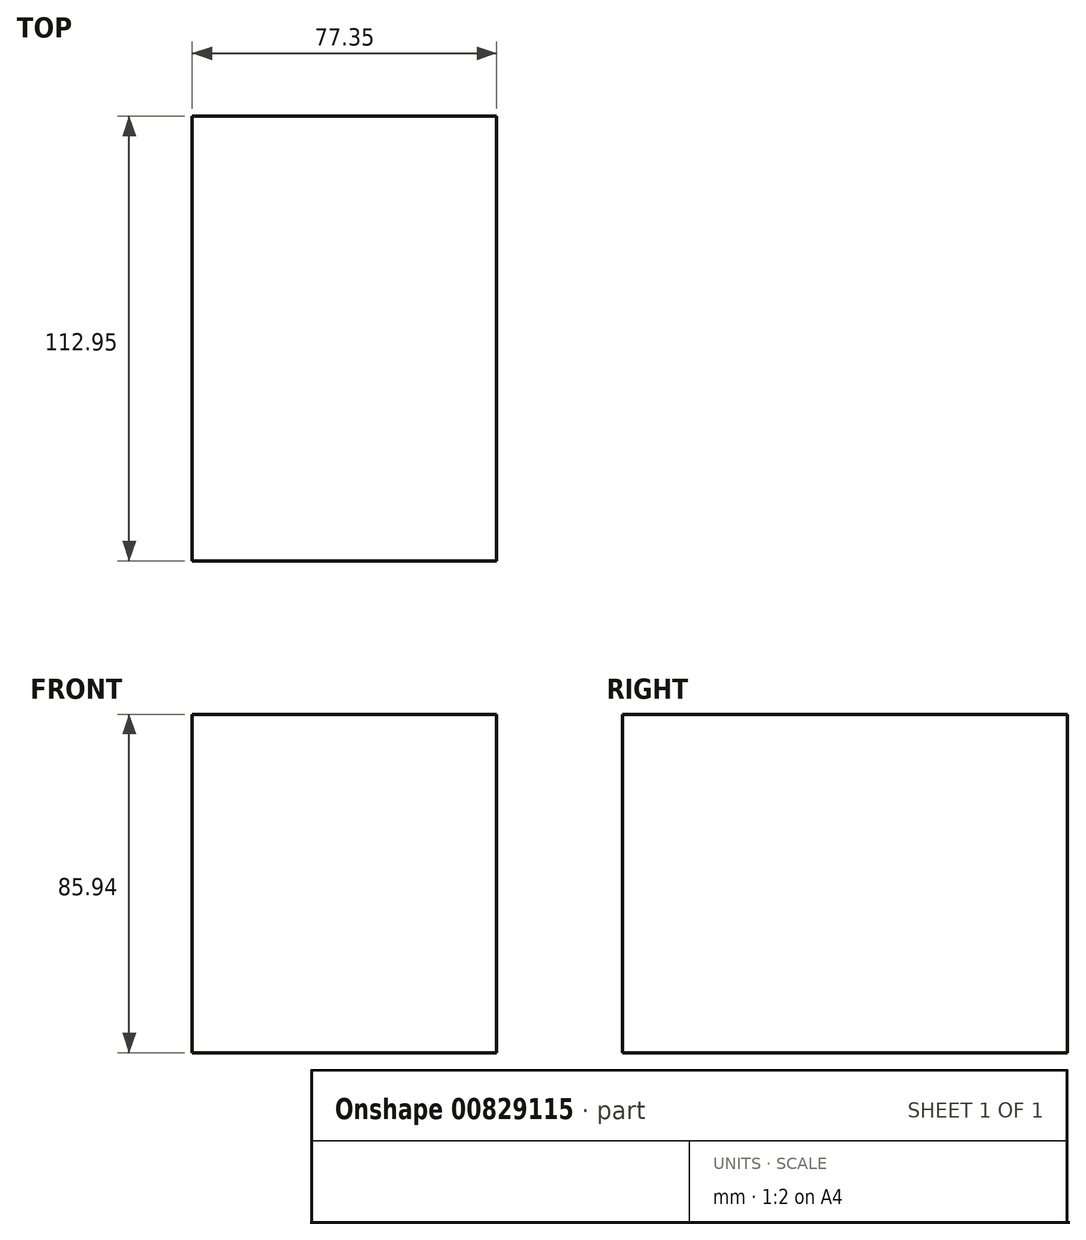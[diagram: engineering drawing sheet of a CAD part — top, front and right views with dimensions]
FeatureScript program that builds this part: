
annotation { "Feature Type Name" : "Feature", "Feature Type Description" : "" }
export const myFeature = defineFeature(function(context is Context, id is Id, definition is map)
    precondition{}
    {
        {
            var Q0;
            Q0=qCreatedBy(makeId("Front.planeOp"),FACE);
            var sketch = newSketch(context, id + "F0", { "sketchPlane" : qUnion([Q0])});
            skLineSegment(sketch, "E0.bottom", {"start": v(50.45, 41.81) * mm, "end": v(-26.9, 41.81) * mm});
            skLineSegment(sketch, "E0.top", {"start": v(50.45, -44.13) * mm, "end": v(-26.9, -44.13) * mm});
            skLineSegment(sketch, "E0.left", {"start": v(50.45, 41.81) * mm, "end": v(50.45, -44.13) * mm});
            skLineSegment(sketch, "E0.right", {"start": v(-26.9, 41.81) * mm, "end": v(-26.9, -44.13) * mm});
            skSolve(sketch);
        }
        {
            var Q0;
            Q0=makeQuery(id+"F0.imprint","IMPRINT",FACE,{"disambiguationData":[TD([[makeQuery(id+"F0.imprint","IMPRINT",EDGE,{"derivedFrom":sQuery(id+"F0.wireOp",EDGE,"E0.bottom")}),1.0]])]});
            extrude(context, id + "F1", {"entities" : qUnion([Q0]), "depth" : 112.95 * mm, "offsetDistance" : 25.4 * mm});
        }
    });
